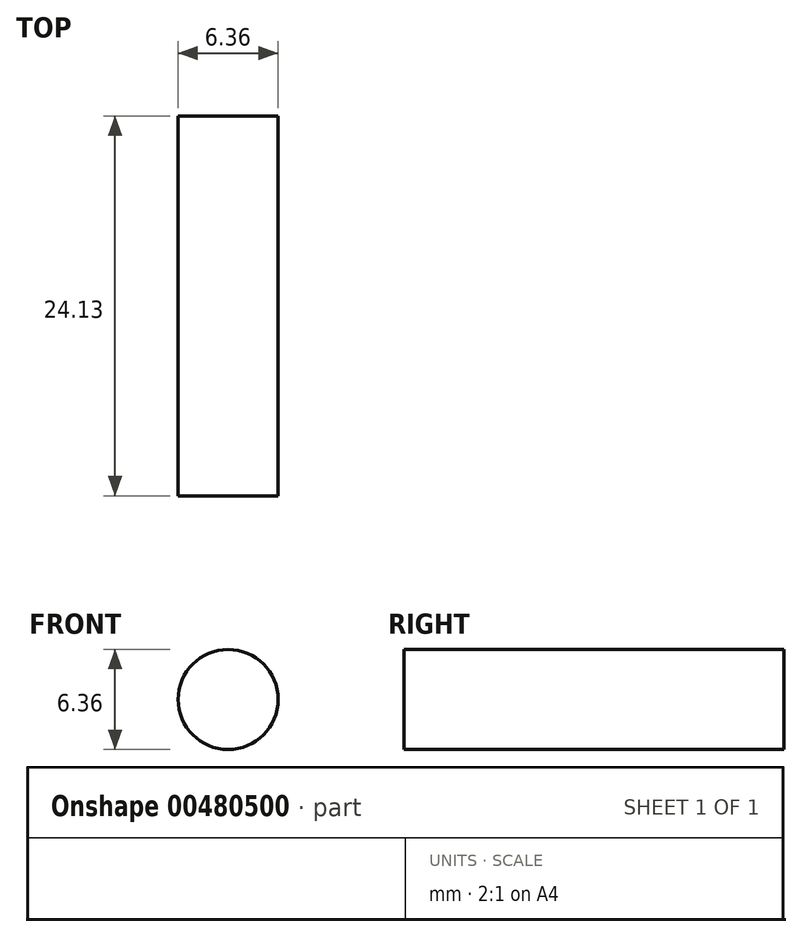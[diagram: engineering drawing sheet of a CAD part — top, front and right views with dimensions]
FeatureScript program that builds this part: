
annotation { "Feature Type Name" : "Feature", "Feature Type Description" : "" }
export const myFeature = defineFeature(function(context is Context, id is Id, definition is map)
    precondition{}
    {
        {
            var Q0;
            Q0=qCreatedBy(makeId("Front.planeOp"),FACE);
            var sketch = newSketch(context, id + "F0", { "sketchPlane" : qUnion([Q0])});
            skCircle(sketch, "E0", {"center": v(0, 0) * mm, "radius": 3.17 * mm});
            skSolve(sketch);
        }
        {
            var Q0;
            Q0 = qSketchRegion(id + "F0", true);
            extrude(context, id + "F1", {"entities" : qUnion([Q0]), "depth" : 24.13 * mm});
        }
    });
